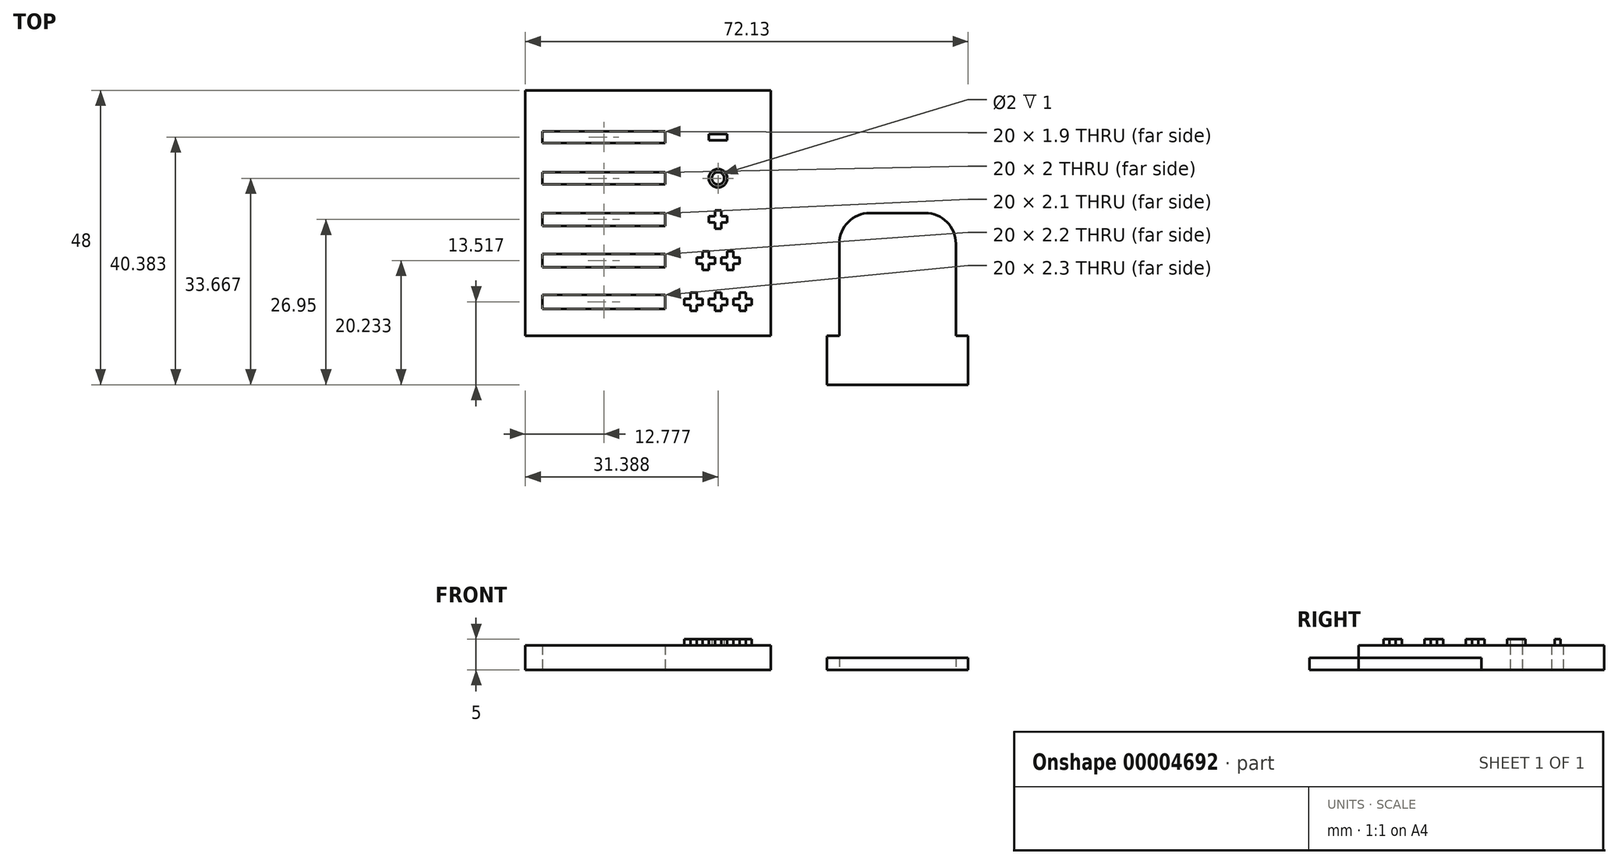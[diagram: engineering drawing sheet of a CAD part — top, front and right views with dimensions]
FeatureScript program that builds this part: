
annotation { "Feature Type Name" : "Feature", "Feature Type Description" : "" }
export const myFeature = defineFeature(function(context is Context, id is Id, definition is map)
    precondition{}
    {
        {
            var Q0;
            Q0=qCreatedBy(makeId("Top.planeOp"),FACE);
            var sketch = newSketch(context, id + "F0", { "sketchPlane" : qUnion([Q0])});
            skLineSegment(sketch, "E0.bottom", {"start": v(20, 0) * mm, "end": v(-20, 0) * mm});
            skLineSegment(sketch, "E0.top", {"start": v(20, 40) * mm, "end": v(-20, 40) * mm});
            skLineSegment(sketch, "E0.left", {"start": v(20, 0) * mm, "end": v(20, 40) * mm});
            skLineSegment(sketch, "E0.right", {"start": v(-20, 0) * mm, "end": v(-20, 40) * mm});
            skLineSegment(sketch, "E1", {"start": v(-20, 40) * mm, "end": v(-8.61, 40) * mm, "construction": true});
            skLineSegment(sketch, "E2", {"start": v(-8.61, 40) * mm, "end": v(2.78, 40) * mm, "construction": true});
            skLineSegment(sketch, "E3", {"start": v(8.61, 80) * mm, "end": v(20, 80) * mm, "construction": true});
            skLineSegment(sketch, "E4", {"start": v(2.78, 40) * mm, "end": v(2.78, 33.33) * mm, "construction": true});
            skLineSegment(sketch, "E5", {"start": v(2.78, 33.33) * mm, "end": v(2.78, 26.67) * mm, "construction": true});
            skLineSegment(sketch, "E6", {"start": v(2.78, 26.67) * mm, "end": v(2.78, 20) * mm, "construction": true});
            skLineSegment(sketch, "E7", {"start": v(2.78, 20) * mm, "end": v(2.78, 13.33) * mm, "construction": true});
            skLineSegment(sketch, "E8", {"start": v(2.78, 13.33) * mm, "end": v(2.78, 6.67) * mm, "construction": true});
            skLineSegment(sketch, "E9", {"start": v(2.78, 6.67) * mm, "end": v(2.78, 0) * mm, "construction": true});
            skLineSegment(sketch, "E10.bottom", {"start": v(2.78, 33.33) * mm, "end": v(-17.22, 33.33) * mm});
            skLineSegment(sketch, "E10.top", {"start": v(2.78, 31.43) * mm, "end": v(-17.22, 31.43) * mm});
            skLineSegment(sketch, "E10.left", {"start": v(2.78, 33.33) * mm, "end": v(2.78, 31.43) * mm});
            skLineSegment(sketch, "E10.right", {"start": v(-17.22, 33.33) * mm, "end": v(-17.22, 31.43) * mm});
            skLineSegment(sketch, "E11.bottom", {"start": v(2.78, 26.67) * mm, "end": v(-17.22, 26.67) * mm});
            skLineSegment(sketch, "E11.top", {"start": v(2.78, 24.67) * mm, "end": v(-17.22, 24.67) * mm});
            skLineSegment(sketch, "E11.left", {"start": v(2.78, 26.67) * mm, "end": v(2.78, 24.67) * mm});
            skLineSegment(sketch, "E11.right", {"start": v(-17.22, 26.67) * mm, "end": v(-17.22, 24.67) * mm});
            skLineSegment(sketch, "E12.bottom", {"start": v(2.78, 20) * mm, "end": v(-17.22, 20) * mm});
            skLineSegment(sketch, "E12.top", {"start": v(2.78, 17.9) * mm, "end": v(-17.22, 17.9) * mm});
            skLineSegment(sketch, "E12.left", {"start": v(2.78, 20) * mm, "end": v(2.78, 17.9) * mm});
            skLineSegment(sketch, "E12.right", {"start": v(-17.22, 20) * mm, "end": v(-17.22, 17.9) * mm});
            skLineSegment(sketch, "E13.bottom", {"start": v(2.78, 13.33) * mm, "end": v(-17.22, 13.33) * mm});
            skLineSegment(sketch, "E13.top", {"start": v(2.78, 11.13) * mm, "end": v(-17.22, 11.13) * mm});
            skLineSegment(sketch, "E13.left", {"start": v(2.78, 13.33) * mm, "end": v(2.78, 11.13) * mm});
            skLineSegment(sketch, "E13.right", {"start": v(-17.22, 13.33) * mm, "end": v(-17.22, 11.13) * mm});
            skLineSegment(sketch, "E14.bottom", {"start": v(2.78, 6.67) * mm, "end": v(-17.22, 6.67) * mm});
            skLineSegment(sketch, "E14.top", {"start": v(2.78, 4.37) * mm, "end": v(-17.22, 4.37) * mm});
            skLineSegment(sketch, "E14.left", {"start": v(2.78, 6.67) * mm, "end": v(2.78, 4.37) * mm});
            skLineSegment(sketch, "E14.right", {"start": v(-17.22, 6.67) * mm, "end": v(-17.22, 4.37) * mm});
            skLineSegment(sketch, "E15", {"start": v(14.3, 80) * mm, "end": v(14.3, 31.43) * mm, "construction": true});
            skLineSegment(sketch, "E16", {"start": v(14.3, 31.43) * mm, "end": v(14.3, 24.67) * mm, "construction": true});
            skLineSegment(sketch, "E17", {"start": v(14.3, 24.67) * mm, "end": v(14.3, 17.9) * mm, "construction": true});
            skLineSegment(sketch, "E18", {"start": v(14.3, 17.9) * mm, "end": v(14.3, 11.13) * mm, "construction": true});
            skLineSegment(sketch, "E19", {"start": v(14.3, 11.13) * mm, "end": v(14.3, 4.37) * mm, "construction": true});
            skLineSegment(sketch, "E20", {"start": v(14.3, 4.37) * mm, "end": v(14.3, 0) * mm, "construction": true});
            skSolve(sketch);
        }
        {
            var Q0;
            Q0 = qSketchRegion(id + "F0", true);
            extrude(context, id + "F1", {"entities" : qUnion([Q0]), "depth" : 4 * mm});
        }
        {
            var Q0;
            Q0=makeQuery(id+"F1.opExtrude","CAP_FACE",FACE,{"disambiguationData":[OSD([sQuery(id+"F0.wireOp",EDGE,"E0.bottom"),sQuery(id+"F0.wireOp",EDGE,"E0.top"),sQuery(id+"F0.wireOp",EDGE,"E0.left"),sQuery(id+"F0.wireOp",EDGE,"E0.right"),sQuery(id+"F0.wireOp",EDGE,"E10.bottom"),sQuery(id+"F0.wireOp",EDGE,"E10.top"),sQuery(id+"F0.wireOp",EDGE,"E10.left"),sQuery(id+"F0.wireOp",EDGE,"E10.right"),sQuery(id+"F0.wireOp",EDGE,"E11.bottom"),sQuery(id+"F0.wireOp",EDGE,"E11.top"),sQuery(id+"F0.wireOp",EDGE,"E11.left"),sQuery(id+"F0.wireOp",EDGE,"E11.right"),sQuery(id+"F0.wireOp",EDGE,"E12.bottom"),sQuery(id+"F0.wireOp",EDGE,"E12.top"),sQuery(id+"F0.wireOp",EDGE,"E12.left"),sQuery(id+"F0.wireOp",EDGE,"E12.right"),sQuery(id+"F0.wireOp",EDGE,"E13.bottom"),sQuery(id+"F0.wireOp",EDGE,"E13.top"),sQuery(id+"F0.wireOp",EDGE,"E13.left"),sQuery(id+"F0.wireOp",EDGE,"E13.right"),sQuery(id+"F0.wireOp",EDGE,"E14.bottom"),sQuery(id+"F0.wireOp",EDGE,"E14.top"),sQuery(id+"F0.wireOp",EDGE,"E14.left"),sQuery(id+"F0.wireOp",EDGE,"E14.right")])],"isStart":false});
            var sketch = newSketch(context, id + "F2", { "sketchPlane" : qUnion([Q0])});
            skLineSegment(sketch, "E21", {"start": v(2.78, 32.38) * mm, "end": v(20, 32.38) * mm, "construction": true});
            skLineSegment(sketch, "E22", {"start": v(2.78, 25.67) * mm, "end": v(20, 25.67) * mm, "construction": true});
            skLineSegment(sketch, "E23", {"start": v(2.78, 18.95) * mm, "end": v(20, 18.95) * mm, "construction": true});
            skLineSegment(sketch, "E24", {"start": v(2.78, 12.23) * mm, "end": v(20, 12.23) * mm, "construction": true});
            skLineSegment(sketch, "E25", {"start": v(2.78, 5.52) * mm, "end": v(20, 5.52) * mm, "construction": true});
            skCircle(sketch, "E26", {"center": v(11.39, 25.67) * mm, "radius": 1.5 * mm});
            skCircle(sketch, "E27", {"center": v(11.39, 25.67) * mm, "radius": 1 * mm});
            skLineSegment(sketch, "E28.bottom", {"start": v(11.89, 20.45) * mm, "end": v(10.89, 20.45) * mm});
            skLineSegment(sketch, "E28.top", {"start": v(11.89, 17.45) * mm, "end": v(10.89, 17.45) * mm});
            skLineSegment(sketch, "E28.left", {"start": v(11.89, 20.45) * mm, "end": v(11.89, 19.45) * mm});
            skLineSegment(sketch, "E28.right", {"start": v(10.89, 20.45) * mm, "end": v(10.89, 19.45) * mm});
            skLineSegment(sketch, "E29.bottom", {"start": v(9.89, 19.45) * mm, "end": v(10.89, 19.45) * mm});
            skLineSegment(sketch, "E29.top", {"start": v(9.89, 18.45) * mm, "end": v(10.89, 18.45) * mm});
            skLineSegment(sketch, "E29.left", {"start": v(9.89, 19.45) * mm, "end": v(9.89, 18.45) * mm});
            skLineSegment(sketch, "E29.right", {"start": v(12.89, 19.45) * mm, "end": v(12.89, 18.45) * mm});
            skLineSegment(sketch, "E30.trimOffspring", {"start": v(10.89, 18.45) * mm, "end": v(10.89, 17.45) * mm});
            skLineSegment(sketch, "E31.trimOffspring", {"start": v(11.89, 19.45) * mm, "end": v(12.89, 19.45) * mm});
            skLineSegment(sketch, "E32.trimOffspring", {"start": v(11.89, 18.45) * mm, "end": v(11.89, 17.45) * mm});
            skLineSegment(sketch, "E33.trimOffspring", {"start": v(11.89, 18.45) * mm, "end": v(12.89, 18.45) * mm});
            skLineSegment(sketch, "E34.bottom", {"start": v(9.89, 13.73) * mm, "end": v(8.89, 13.73) * mm});
            skLineSegment(sketch, "E34.top", {"start": v(9.89, 10.73) * mm, "end": v(8.89, 10.73) * mm});
            skLineSegment(sketch, "E34.left", {"start": v(9.89, 13.73) * mm, "end": v(9.89, 12.73) * mm});
            skLineSegment(sketch, "E34.right", {"start": v(8.89, 13.73) * mm, "end": v(8.89, 12.73) * mm});
            skLineSegment(sketch, "E35.bottom", {"start": v(7.89, 12.73) * mm, "end": v(8.89, 12.73) * mm});
            skLineSegment(sketch, "E35.top", {"start": v(7.89, 11.73) * mm, "end": v(8.89, 11.73) * mm});
            skLineSegment(sketch, "E35.left", {"start": v(7.89, 12.73) * mm, "end": v(7.89, 11.73) * mm});
            skLineSegment(sketch, "E35.right", {"start": v(10.89, 12.73) * mm, "end": v(10.89, 11.73) * mm});
            skLineSegment(sketch, "E36.bottom", {"start": v(13.89, 13.73) * mm, "end": v(12.89, 13.73) * mm});
            skLineSegment(sketch, "E36.top", {"start": v(13.89, 10.73) * mm, "end": v(12.89, 10.73) * mm});
            skLineSegment(sketch, "E36.left", {"start": v(13.89, 13.73) * mm, "end": v(13.89, 12.73) * mm});
            skLineSegment(sketch, "E36.right", {"start": v(12.89, 13.73) * mm, "end": v(12.89, 12.73) * mm});
            skLineSegment(sketch, "E37.bottom", {"start": v(11.89, 12.73) * mm, "end": v(12.89, 12.73) * mm});
            skLineSegment(sketch, "E37.top", {"start": v(11.89, 11.73) * mm, "end": v(12.89, 11.73) * mm});
            skLineSegment(sketch, "E37.left", {"start": v(11.89, 12.73) * mm, "end": v(11.89, 11.73) * mm});
            skLineSegment(sketch, "E37.right", {"start": v(14.89, 12.73) * mm, "end": v(14.89, 11.73) * mm});
            skLineSegment(sketch, "E38.bottom", {"start": v(7.89, 7.02) * mm, "end": v(6.89, 7.02) * mm});
            skLineSegment(sketch, "E38.top", {"start": v(7.89, 4.02) * mm, "end": v(6.89, 4.02) * mm});
            skLineSegment(sketch, "E38.left", {"start": v(7.89, 7.02) * mm, "end": v(7.89, 6.02) * mm});
            skLineSegment(sketch, "E38.right", {"start": v(6.89, 7.02) * mm, "end": v(6.89, 6.02) * mm});
            skLineSegment(sketch, "E39.bottom", {"start": v(5.89, 6.02) * mm, "end": v(6.89, 6.02) * mm});
            skLineSegment(sketch, "E39.top", {"start": v(5.89, 5.02) * mm, "end": v(6.89, 5.02) * mm});
            skLineSegment(sketch, "E39.left", {"start": v(5.89, 6.02) * mm, "end": v(5.89, 5.02) * mm});
            skLineSegment(sketch, "E39.right", {"start": v(8.89, 6.02) * mm, "end": v(8.89, 5.02) * mm});
            skLineSegment(sketch, "E40.bottom", {"start": v(11.89, 7.02) * mm, "end": v(10.89, 7.02) * mm});
            skLineSegment(sketch, "E40.top", {"start": v(11.89, 4.02) * mm, "end": v(10.89, 4.02) * mm});
            skLineSegment(sketch, "E40.left", {"start": v(11.89, 7.02) * mm, "end": v(11.89, 6.02) * mm});
            skLineSegment(sketch, "E40.right", {"start": v(10.89, 7.02) * mm, "end": v(10.89, 6.02) * mm});
            skLineSegment(sketch, "E41.bottom", {"start": v(9.89, 6.02) * mm, "end": v(10.89, 6.02) * mm});
            skLineSegment(sketch, "E41.top", {"start": v(9.89, 5.02) * mm, "end": v(10.89, 5.02) * mm});
            skLineSegment(sketch, "E41.left", {"start": v(9.89, 6.02) * mm, "end": v(9.89, 5.02) * mm});
            skLineSegment(sketch, "E41.right", {"start": v(12.89, 6.02) * mm, "end": v(12.89, 5.02) * mm});
            skLineSegment(sketch, "E42.trimOffspring", {"start": v(9.89, 12.73) * mm, "end": v(10.89, 12.73) * mm});
            skLineSegment(sketch, "E43.trimOffspring", {"start": v(8.89, 11.73) * mm, "end": v(8.89, 10.73) * mm});
            skLineSegment(sketch, "E44.trimOffspring", {"start": v(9.89, 11.73) * mm, "end": v(10.89, 11.73) * mm});
            skLineSegment(sketch, "E45.trimOffspring", {"start": v(9.89, 11.73) * mm, "end": v(9.89, 10.73) * mm});
            skLineSegment(sketch, "E46.trimOffspring", {"start": v(12.89, 11.73) * mm, "end": v(12.89, 10.73) * mm});
            skLineSegment(sketch, "E47.trimOffspring", {"start": v(13.89, 12.73) * mm, "end": v(14.89, 12.73) * mm});
            skLineSegment(sketch, "E48.trimOffspring", {"start": v(13.89, 11.73) * mm, "end": v(13.89, 10.73) * mm});
            skLineSegment(sketch, "E49.trimOffspring", {"start": v(13.89, 11.73) * mm, "end": v(14.89, 11.73) * mm});
            skLineSegment(sketch, "E50.trimOffspring", {"start": v(7.89, 6.02) * mm, "end": v(8.89, 6.02) * mm});
            skLineSegment(sketch, "E51.trimOffspring", {"start": v(7.89, 5.02) * mm, "end": v(7.89, 4.02) * mm});
            skLineSegment(sketch, "E52.trimOffspring", {"start": v(7.89, 5.02) * mm, "end": v(8.89, 5.02) * mm});
            skLineSegment(sketch, "E53.trimOffspring", {"start": v(6.89, 5.02) * mm, "end": v(6.89, 4.02) * mm});
            skLineSegment(sketch, "E54.trimOffspring", {"start": v(10.89, 5.02) * mm, "end": v(10.89, 4.02) * mm});
            skLineSegment(sketch, "E55.trimOffspring", {"start": v(11.89, 6.02) * mm, "end": v(12.89, 6.02) * mm});
            skLineSegment(sketch, "E56.trimOffspring", {"start": v(11.89, 5.02) * mm, "end": v(11.89, 4.02) * mm});
            skLineSegment(sketch, "E57.trimOffspring", {"start": v(11.89, 5.02) * mm, "end": v(12.89, 5.02) * mm});
            skPoint(sketch, "E58", {"position": v(14.89, 12.23) * mm});
            skLineSegment(sketch, "E59", {"start": v(10.89, 18.45) * mm, "end": v(11.89, 19.45) * mm, "construction": true});
            skPoint(sketch, "E60", {"position": v(11.39, 18.95) * mm});
            skLineSegment(sketch, "E61", {"start": v(13.89, 12.73) * mm, "end": v(12.89, 11.73) * mm, "construction": true});
            skPoint(sketch, "E62", {"position": v(13.39, 12.23) * mm});
            skLineSegment(sketch, "E63.bottom", {"start": v(9.89, 32.88) * mm, "end": v(12.89, 32.88) * mm});
            skLineSegment(sketch, "E63.top", {"start": v(9.89, 31.88) * mm, "end": v(12.89, 31.88) * mm});
            skLineSegment(sketch, "E63.left", {"start": v(9.89, 32.88) * mm, "end": v(9.89, 31.88) * mm});
            skLineSegment(sketch, "E63.right", {"start": v(12.89, 32.88) * mm, "end": v(12.89, 31.88) * mm});
            skLineSegment(sketch, "E64", {"start": v(9.89, 31.88) * mm, "end": v(12.89, 32.88) * mm, "construction": true});
            skPoint(sketch, "E65", {"position": v(11.39, 32.38) * mm});
            skLineSegment(sketch, "E66.bottom", {"start": v(13.89, 6.02) * mm, "end": v(14.89, 6.02) * mm});
            skLineSegment(sketch, "E66.top", {"start": v(13.89, 5.02) * mm, "end": v(14.89, 5.02) * mm});
            skLineSegment(sketch, "E66.left", {"start": v(13.89, 6.02) * mm, "end": v(13.89, 5.02) * mm});
            skLineSegment(sketch, "E66.right", {"start": v(16.89, 6.02) * mm, "end": v(16.89, 5.02) * mm});
            skLineSegment(sketch, "E67.bottom", {"start": v(14.89, 7.02) * mm, "end": v(15.89, 7.02) * mm});
            skLineSegment(sketch, "E67.top", {"start": v(14.89, 4.02) * mm, "end": v(15.89, 4.02) * mm});
            skLineSegment(sketch, "E67.left", {"start": v(14.89, 7.02) * mm, "end": v(14.89, 6.02) * mm});
            skLineSegment(sketch, "E67.right", {"start": v(15.89, 7.02) * mm, "end": v(15.89, 6.02) * mm});
            skLineSegment(sketch, "E68.trimOffspring", {"start": v(14.89, 5.02) * mm, "end": v(14.89, 4.02) * mm});
            skLineSegment(sketch, "E69.trimOffspring", {"start": v(15.89, 6.02) * mm, "end": v(16.89, 6.02) * mm});
            skLineSegment(sketch, "E70.trimOffspring", {"start": v(15.89, 5.02) * mm, "end": v(15.89, 4.02) * mm});
            skLineSegment(sketch, "E71.trimOffspring", {"start": v(15.89, 5.02) * mm, "end": v(16.89, 5.02) * mm});
            skPoint(sketch, "E72", {"position": v(16.89, 5.52) * mm});
            skSolve(sketch);
        }
        {
            var Q0;
            Q0 = qSketchRegion(id + "F2", true);
            extrude(context, id + "F3", {"entities" : qUnion([Q0]), "operationType" : NewBodyOperationType.ADD, "depth" : 1 * mm});
        }
        {
            var Q0;
            Q0=qCreatedBy(makeId("Top.planeOp"),FACE);
            var sketch = newSketch(context, id + "F4", { "sketchPlane" : qUnion([Q0])});
            skLineSegment(sketch, "E73.top", {"start": v(36.13, 20) * mm, "end": v(45.13, 20) * mm});
            skLineSegment(sketch, "E73.left", {"start": v(31.13, 0) * mm, "end": v(31.13, 15) * mm});
            skLineSegment(sketch, "E73.right", {"start": v(50.13, 0) * mm, "end": v(50.13, 15) * mm});
            skLineSegment(sketch, "E74.bottom", {"start": v(29.13, 0) * mm, "end": v(31.13, 0) * mm});
            skLineSegment(sketch, "E74.top", {"start": v(29.13, -8) * mm, "end": v(52.13, -8) * mm});
            skLineSegment(sketch, "E74.left", {"start": v(29.13, 0) * mm, "end": v(29.13, -8) * mm});
            skLineSegment(sketch, "E74.right", {"start": v(52.13, 0) * mm, "end": v(52.13, -8) * mm});
            skLineSegment(sketch, "E75.trimOffspring", {"start": v(50.13, 0) * mm, "end": v(52.13, 0) * mm});
            skPoint(sketch, "E76.visualSharp", {"position": v(31.13, 20) * mm});
            skArc(sketch, "E76.filletArc", {"start": v(36.13, 20) * mm, "mid": v(32.6, 18.54) * mm, "end": v(31.13, 15) * mm});
            skPoint(sketch, "E77.visualSharp", {"position": v(50.13, 20) * mm});
            skArc(sketch, "E77.filletArc", {"start": v(50.13, 15) * mm, "mid": v(48.67, 18.54) * mm, "end": v(45.13, 20) * mm});
            skSolve(sketch);
        }
        {
            var Q0;
            Q0=makeQuery(id+"F4.imprint","IMPRINT",FACE,{"disambiguationData":[TD([[makeQuery(id+"F4.imprint","IMPRINT",EDGE,{"derivedFrom":sQuery(id+"F4.wireOp",EDGE,"E73.top")}),-1.0]])]});
            extrude(context, id + "F5", {"entities" : qUnion([Q0]), "depth" : 2 * mm});
        }
    });
